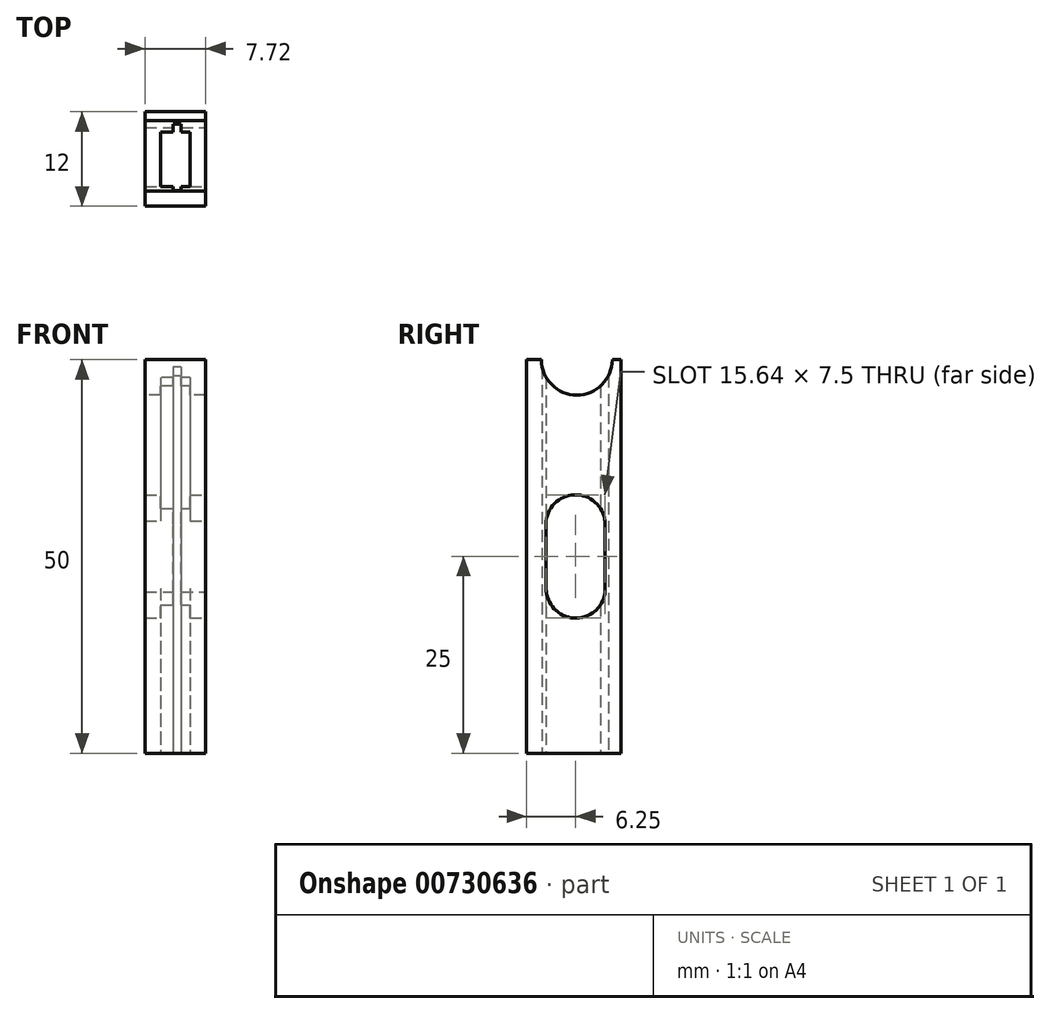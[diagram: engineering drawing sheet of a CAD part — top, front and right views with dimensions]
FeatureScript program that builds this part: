
annotation { "Feature Type Name" : "Feature", "Feature Type Description" : "" }
export const myFeature = defineFeature(function(context is Context, id is Id, definition is map)
    precondition{}
    {
        {
            var Q0;
            Q0=qCreatedBy(makeId("Top.planeOp"),FACE);
            var sketch = newSketch(context, id + "F0", { "sketchPlane" : qUnion([Q0])});
            skLineSegment(sketch, "E0.bottom", {"start": v(-0.53, 4) * mm, "end": v(0.47, 4) * mm});
            skLineSegment(sketch, "E0.top", {"start": v(-0.53, -4.4) * mm, "end": v(0.47, -4.4) * mm});
            skLineSegment(sketch, "E1.left", {"start": v(-0.53, 4) * mm, "end": v(-0.53, 3) * mm});
            skLineSegment(sketch, "E1.right", {"start": v(0.47, 4) * mm, "end": v(0.47, 3) * mm});
            skLineSegment(sketch, "E2", {"start": v(-2.2, 3) * mm, "end": v(2.16, 3) * mm, "construction": true});
            skLineSegment(sketch, "E3", {"start": v(-2.3, -3.9) * mm, "end": v(2.6, -3.9) * mm, "construction": true});
            skLineSegment(sketch, "E4", {"start": v(-0.53, 3) * mm, "end": v(-2.12, 3) * mm});
            skLineSegment(sketch, "E5", {"start": v(0.47, 3) * mm, "end": v(1.6, 3) * mm});
            skLineSegment(sketch, "E6", {"start": v(-0.53, -3.9) * mm, "end": v(-2.12, -3.9) * mm});
            skLineSegment(sketch, "E7", {"start": v(0.47, -3.9) * mm, "end": v(1.6, -3.9) * mm});
            skLineSegment(sketch, "E8.trimOffspring", {"start": v(-0.53, -3.9) * mm, "end": v(-0.53, -4.4) * mm});
            skLineSegment(sketch, "E9.trimOffspring", {"start": v(0.47, -3.9) * mm, "end": v(0.47, -4.4) * mm});
            skLineSegment(sketch, "E10.top", {"start": v(-2.12, 5.6) * mm, "end": v(1.6, 5.6) * mm});
            skLineSegment(sketch, "E11.top", {"start": v(-2.12, -6.4) * mm, "end": v(1.6, -6.4) * mm});
            skLineSegment(sketch, "E12.bottom", {"start": v(-2.12, 5.6) * mm, "end": v(-4.12, 5.6) * mm});
            skLineSegment(sketch, "E12.top", {"start": v(-2.12, -6.4) * mm, "end": v(-4.12, -6.4) * mm});
            skLineSegment(sketch, "E12.left", {"start": v(-2.12, 3) * mm, "end": v(-2.12, -3.9) * mm});
            skLineSegment(sketch, "E12.right", {"start": v(-4.12, 5.6) * mm, "end": v(-4.12, -6.4) * mm});
            skLineSegment(sketch, "E13.bottom", {"start": v(1.6, 5.6) * mm, "end": v(3.6, 5.6) * mm});
            skLineSegment(sketch, "E13.top", {"start": v(1.6, -6.4) * mm, "end": v(3.6, -6.4) * mm});
            skLineSegment(sketch, "E13.right", {"start": v(3.6, 5.6) * mm, "end": v(3.6, -6.4) * mm});
            skPoint(sketch, "E14.orphan", {"position": v(1.6, -4.4) * mm});
            skLineSegment(sketch, "E15.trimOffspring", {"start": v(1.6, 3) * mm, "end": v(1.6, -3.9) * mm});
            skPoint(sketch, "E16.orphan", {"position": v(1.6, 4) * mm});
            skSolve(sketch);
        }
        {
            var Q0;
            Q0=makeQuery(id+"F0.imprint","IMPRINT",FACE,{"disambiguationData":[TD([[makeQuery(id+"F0.imprint","IMPRINT",EDGE,{"derivedFrom":sQuery(id+"F0.wireOp",EDGE,"E1.left")}),-1.0]])]});
            extrude(context, id + "F1", {"entities" : qUnion([Q0]), "depth" : 50 * mm, "offsetDistance" : 25 * mm});
        }
        {
            var Q0;
            Q0=makeQuery(id+"F1.opExtrude","SWEPT_FACE",FACE,{"disambiguationData":[OSD([sQuery(id+"F0.wireOp",EDGE,"E13.right")])]});
            var sketch = newSketch(context, id + "F2", { "sketchPlane" : qUnion([Q0])});
            skLineSegment(sketch, "E17.left", {"start": v(-3.9, 20.94) * mm, "end": v(-3.9, 29.52) * mm});
            skLineSegment(sketch, "E17.right", {"start": v(3.6, 20.48) * mm, "end": v(3.6, 29.06) * mm});
            skPoint(sketch, "E17.middle", {"position": v(-0.15, 25) * mm});
            skArc(sketch, "E18", {"start": v(3.6, 29.06) * mm, "mid": v(0.07, 32.82) * mm, "end": v(-3.9, 29.52) * mm});
            skArc(sketch, "E19", {"start": v(-3.9, 20.94) * mm, "mid": v(-0.37, 17.18) * mm, "end": v(3.6, 20.48) * mm});
            skSolve(sketch);
        }
        {
            var Q0;
            Q0=makeQuery(id+"F2.imprint","IMPRINT",FACE,{"disambiguationData":[TD([[makeQuery(id+"F2.imprint","IMPRINT",EDGE,{"derivedFrom":sQuery(id+"F2.wireOp",EDGE,"E17.left")}),-1.0]])]});
            extrude(context, id + "F3", {"entities" : qUnion([Q0]), "operationType" : NewBodyOperationType.REMOVE, "oppositeDirection" : true, "depth" : 25 * mm, "offsetDistance" : 25 * mm});
        }
        {
            var Q0;
            Q0=makeQuery(id+"F1.opExtrude","SWEPT_FACE",FACE,{"disambiguationData":[OSD([sQuery(id+"F0.wireOp",EDGE,"E12.right")])]});
            var sketch = newSketch(context, id + "F4", { "sketchPlane" : qUnion([Q0])});
            skCircle(sketch, "E20", {"center": v(0, 50) * mm, "radius": 4.5 * mm});
            skPoint(sketch, "E20.centerSnap0", {"position": v(0.4, 50) * mm});
            skSolve(sketch);
        }
        {
            var Q0;
            Q0 = qSketchRegion(id + "F4", true);
            extrude(context, id + "F5", {"entities" : qUnion([Q0]), "operationType" : NewBodyOperationType.REMOVE, "oppositeDirection" : true, "depth" : 25 * mm, "offsetDistance" : 25 * mm});
        }
    });
